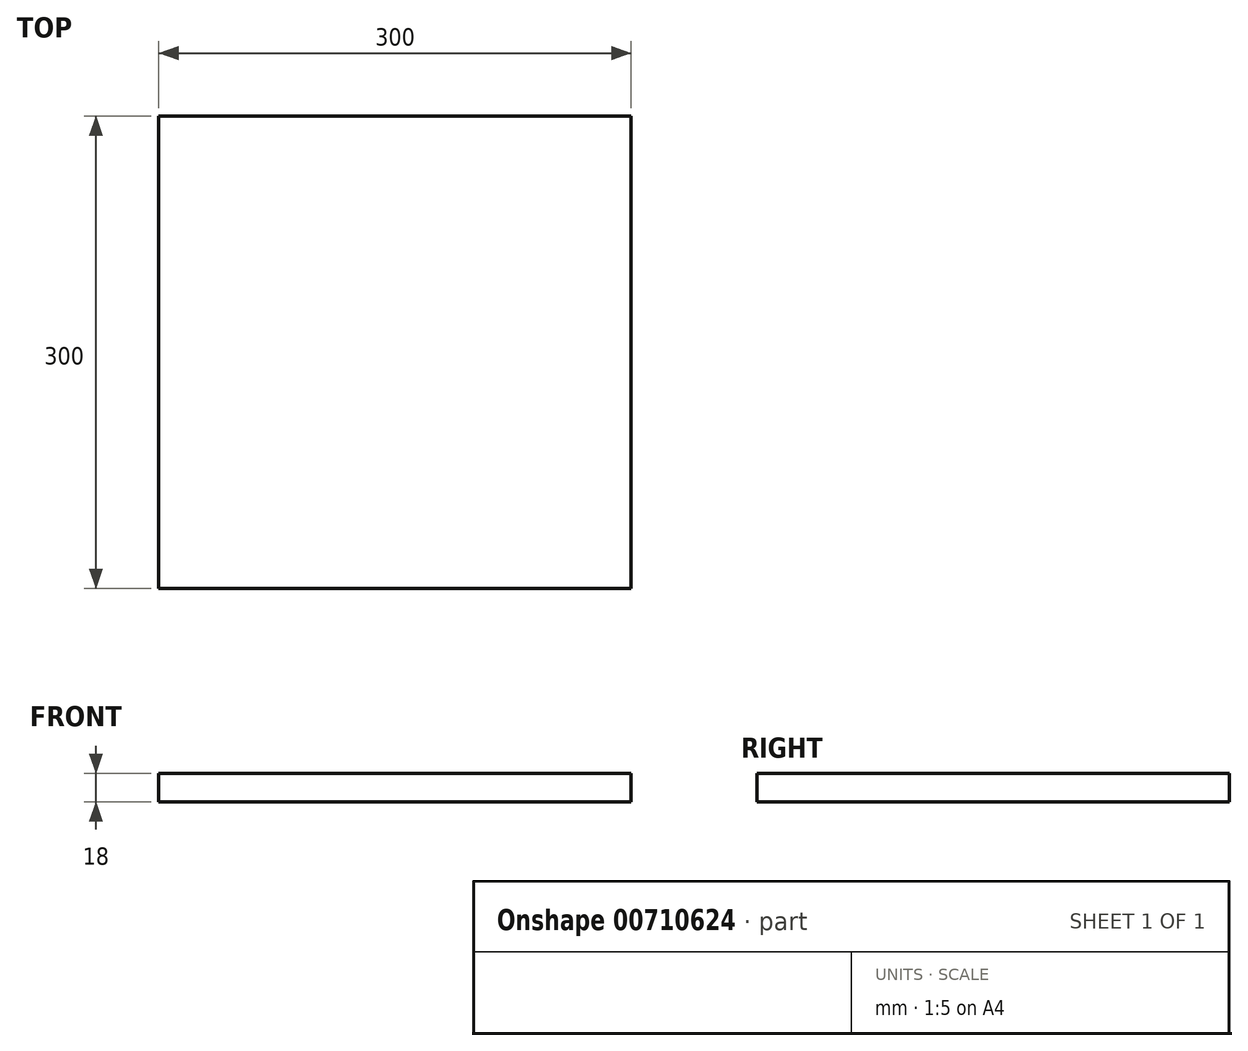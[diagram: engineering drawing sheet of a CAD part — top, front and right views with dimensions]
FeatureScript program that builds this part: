
annotation { "Feature Type Name" : "Feature", "Feature Type Description" : "" }
export const myFeature = defineFeature(function(context is Context, id is Id, definition is map)
    precondition{}
    {
        {
            var Q0;
            Q0=qCreatedBy(makeId("Top.planeOp"),FACE);
            var sketch = newSketch(context, id + "F0", { "sketchPlane" : qUnion([Q0])});
            skLineSegment(sketch, "E0.bottom", {"start": v(0, 0) * mm, "end": v(300, 0) * mm});
            skLineSegment(sketch, "E0.top", {"start": v(0, 300) * mm, "end": v(300, 300) * mm});
            skLineSegment(sketch, "E0.left", {"start": v(0, 0) * mm, "end": v(0, 300) * mm});
            skLineSegment(sketch, "E0.right", {"start": v(300, 0) * mm, "end": v(300, 300) * mm});
            skSolve(sketch);
        }
        {
            var Q0;
            Q0=makeQuery(id+"F0.imprint","IMPRINT",FACE,{"disambiguationData":[TD([[makeQuery(id+"F0.imprint","IMPRINT",EDGE,{"derivedFrom":sQuery(id+"F0.wireOp",EDGE,"E0.bottom")}),1.0]])]});
            extrude(context, id + "F1", {"entities" : qUnion([Q0]), "depth" : 18 * mm, "offsetDistance" : 25 * mm});
        }
    });
